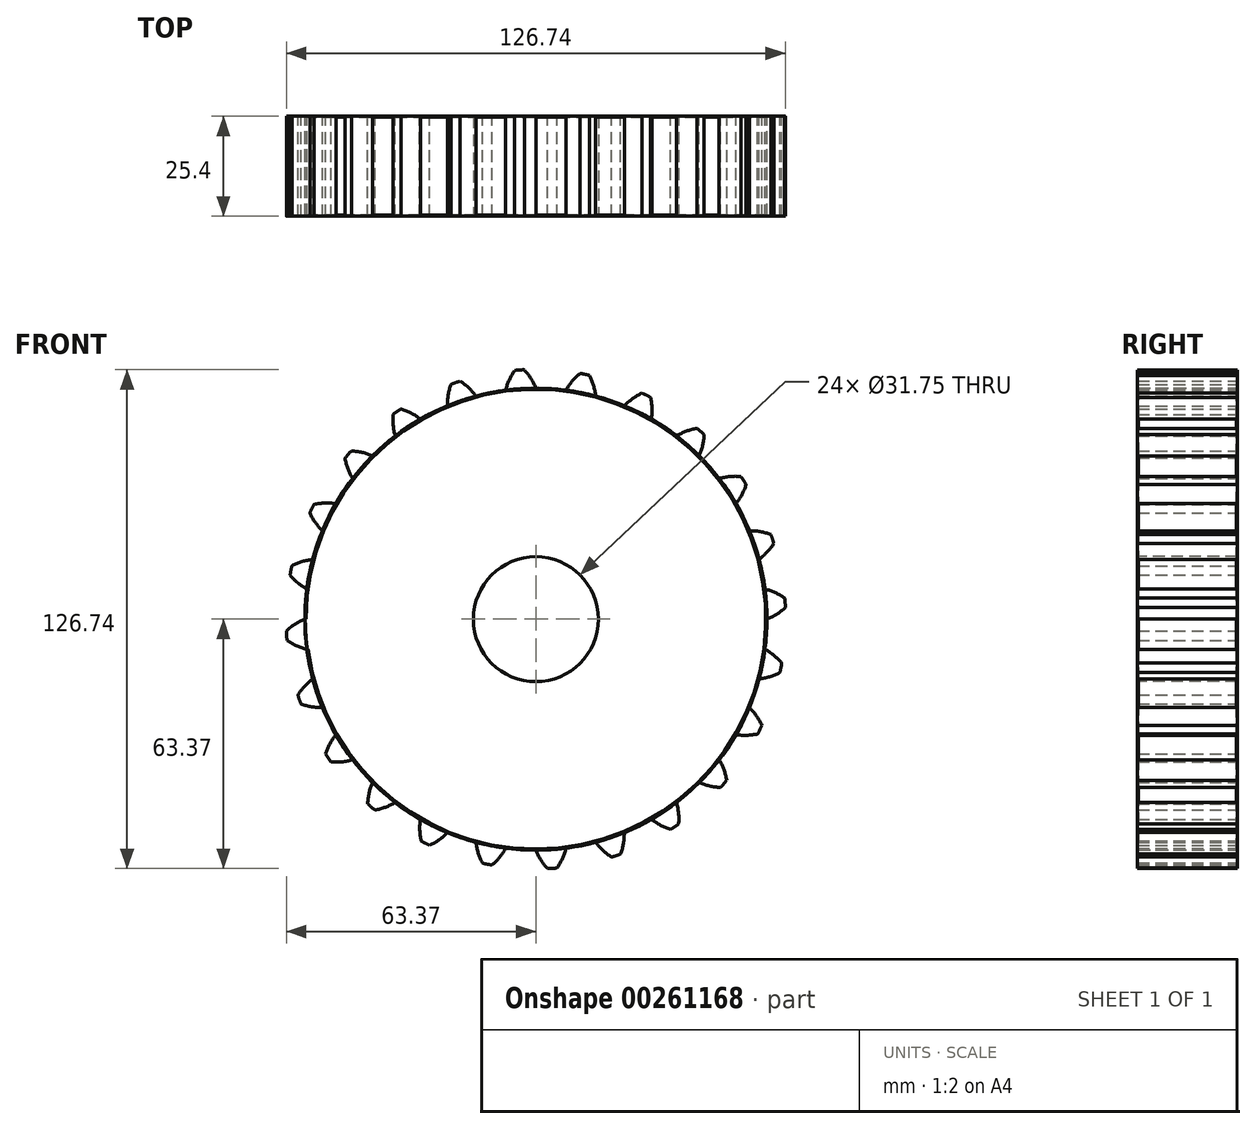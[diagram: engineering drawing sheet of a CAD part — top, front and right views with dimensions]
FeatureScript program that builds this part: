
annotation { "Feature Type Name" : "Feature", "Feature Type Description" : "" }
export const myFeature = defineFeature(function(context is Context, id is Id, definition is map)
    precondition{}
    {
        {
            var Q0;
            Q0=qCreatedBy(makeId("Front.planeOp"),FACE);
            var sketch = newSketch(context, id + "F0", { "sketchPlane" : qUnion([Q0])});
            skCircle(sketch, "E0", {"center": v(0, 0) * mm, "radius": 63.5 * mm, "construction": true});
            skCircle(sketch, "E1", {"center": v(0, 0) * mm, "radius": 53.72 * mm, "construction": true});
            skCircle(sketch, "E2", {"center": v(0, 0) * mm, "radius": 58.67 * mm});
            skLineSegment(sketch, "E3", {"start": v(0, 0) * mm, "end": v(0, 96.68) * mm, "construction": true});
            skLineSegment(sketch, "E4", {"start": v(0, 0) * mm, "end": v(-6.34, 96.72) * mm, "construction": true});
            skLineSegment(sketch, "E5", {"start": v(0, 58.67) * mm, "end": v(-75.78, 58.67) * mm, "construction": true});
            skLineSegment(sketch, "E6", {"start": v(0, 58.67) * mm, "end": v(-75.78, 31.1) * mm, "construction": true});
            skCircle(sketch, "E7", {"center": v(0, 0) * mm, "radius": 55.14 * mm, "construction": true});
            skCircle(sketch, "E8", {"center": v(0, 58.67) * mm, "radius": 14.6 * mm, "construction": true});
            skCircle(sketch, "E9", {"center": v(-13.63, 53.42) * mm, "radius": 14.6 * mm, "construction": true});
            skArc(sketch, "E10", {"start": v(0, 58.67) * mm, "mid": v(-1.24, 61.16) * mm, "end": v(-2.93, 63.37) * mm});
            skArc(sketch, "E11", {"start": v(0.97, 53.71) * mm, "mid": v(0.7, 56.24) * mm, "end": v(0, 58.67) * mm});
            skArc(sketch, "E12.MirrorCS", {"start": v(-7.66, 58.17) * mm, "mid": v(-6.75, 60.8) * mm, "end": v(-5.37, 63.2) * mm});
            skArc(sketch, "E13.MirrorCS", {"start": v(-7.98, 53.13) * mm, "mid": v(-8.04, 55.66) * mm, "end": v(-7.66, 58.17) * mm});
            skArc(sketch, "E14", {"start": v(-2.93, 63.37) * mm, "mid": v(-4.15, 63.34) * mm, "end": v(-5.37, 63.2) * mm});
            skSolve(sketch);
        }
        {
            var Q0;
            {var subQ0=sQuery(id+"F0.wireOp",EDGE,"E10");Q0=makeQuery(id+"F0.imprint","IMPRINT",FACE,{"disambiguationData":[TD([[makeQuery(id+"F0.imprint","IMPRINT",EDGE,{"derivedFrom":subQ0}),1.0]])]});}
            var Q1;
            {var subQ0=sQuery(id+"F0.wireOp",EDGE,"E2");var subQ1=makeQuery(id+"F0.imprint","INTERSECT",VERTEX,{"derivedFrom":[subQ0,sQuery(id+"F0.wireOp",EDGE,"E10")]});Q1=makeQuery(id+"F0.imprint","IMPRINT",FACE,{"disambiguationData":[TD([[makeQuery(id+"F0.imprint","IMPRINT",EDGE,{"disambiguationData":[TD([[subQ1,-1.0]])],"derivedFrom":subQ0}),1.0]])]});}
            extrude(context, id + "F1", {"entities" : qUnion([Q0, Q1]), "endBound" : BoundingType.SYMMETRIC, "depth" : 25.4 * mm});
        }
        {
            var Q0;
            Q0=makeQuery(id+"F1.opExtrude","SWEPT_BODY",BODY,{"disambiguationData":[OSD([sQuery(id+"F0.wireOp",EDGE,"E2"),sQuery(id+"F0.wireOp",EDGE,"E10"),sQuery(id+"F0.wireOp",EDGE,"E12.MirrorCS"),sQuery(id+"F0.wireOp",EDGE,"E14")])]});
            var Q1;
            Q1=makeQuery(id+"F1.opExtrude","SWEPT_FACE",FACE,{"disambiguationData":[OSD([sQuery(id+"F0.wireOp",EDGE,"E2")])]});
            circularPattern(context, id + "F2", {"entities" : qUnion([Q0]), "axis" : qUnion([Q1]), "angle" : 15 * degree, "instanceCount" : 24});
        }
        {
            var Q0;
            Q0=makeQuery(id+"F2.opPattern","COPY",FACE,{"derivedFrom":makeQuery(id+"F1.opExtrude","CAP_FACE",FACE,{"disambiguationData":[OSD([sQuery(id+"F0.wireOp",EDGE,"E2"),sQuery(id+"F0.wireOp",EDGE,"E10"),sQuery(id+"F0.wireOp",EDGE,"E12.MirrorCS"),sQuery(id+"F0.wireOp",EDGE,"E14")])],"isStart":false}),"instanceName":"12"});
            var sketch = newSketch(context, id + "F3", { "sketchPlane" : qUnion([Q0])});
            skCircle(sketch, "E15", {"center": v(0, 0) * mm, "radius": 15.24 * mm});
            skSolve(sketch);
        }
        {
            var Q0;
            Q0=sQuery(id+"F3.wireOp",VERTEX,"E15.center");
            var Q1;
            Q1=makeQuery(id+"F1.opExtrude","SWEPT_BODY",BODY,{"disambiguationData":[OSD([sQuery(id+"F0.wireOp",EDGE,"E2"),sQuery(id+"F0.wireOp",EDGE,"E10"),sQuery(id+"F0.wireOp",EDGE,"E12.MirrorCS"),sQuery(id+"F0.wireOp",EDGE,"E14")])]});
            var Q2;
            Q2=makeQuery(id+"F2.opPattern","COPY",BODY,{"derivedFrom":makeQuery(id+"F1.opExtrude","SWEPT_BODY",BODY,{"disambiguationData":[OSD([sQuery(id+"F0.wireOp",EDGE,"E2"),sQuery(id+"F0.wireOp",EDGE,"E10"),sQuery(id+"F0.wireOp",EDGE,"E12.MirrorCS"),sQuery(id+"F0.wireOp",EDGE,"E14")])]}),"instanceName":"1"});
            var Q3;
            Q3=makeQuery(id+"F2.opPattern","COPY",BODY,{"derivedFrom":makeQuery(id+"F1.opExtrude","SWEPT_BODY",BODY,{"disambiguationData":[OSD([sQuery(id+"F0.wireOp",EDGE,"E2"),sQuery(id+"F0.wireOp",EDGE,"E10"),sQuery(id+"F0.wireOp",EDGE,"E12.MirrorCS"),sQuery(id+"F0.wireOp",EDGE,"E14")])]}),"instanceName":"2"});
            var Q4;
            Q4=makeQuery(id+"F2.opPattern","COPY",BODY,{"derivedFrom":makeQuery(id+"F1.opExtrude","SWEPT_BODY",BODY,{"disambiguationData":[OSD([sQuery(id+"F0.wireOp",EDGE,"E2"),sQuery(id+"F0.wireOp",EDGE,"E10"),sQuery(id+"F0.wireOp",EDGE,"E12.MirrorCS"),sQuery(id+"F0.wireOp",EDGE,"E14")])]}),"instanceName":"3"});
            var Q5;
            Q5=makeQuery(id+"F2.opPattern","COPY",BODY,{"derivedFrom":makeQuery(id+"F1.opExtrude","SWEPT_BODY",BODY,{"disambiguationData":[OSD([sQuery(id+"F0.wireOp",EDGE,"E2"),sQuery(id+"F0.wireOp",EDGE,"E10"),sQuery(id+"F0.wireOp",EDGE,"E12.MirrorCS"),sQuery(id+"F0.wireOp",EDGE,"E14")])]}),"instanceName":"4"});
            var Q6;
            Q6=makeQuery(id+"F2.opPattern","COPY",BODY,{"derivedFrom":makeQuery(id+"F1.opExtrude","SWEPT_BODY",BODY,{"disambiguationData":[OSD([sQuery(id+"F0.wireOp",EDGE,"E2"),sQuery(id+"F0.wireOp",EDGE,"E10"),sQuery(id+"F0.wireOp",EDGE,"E12.MirrorCS"),sQuery(id+"F0.wireOp",EDGE,"E14")])]}),"instanceName":"5"});
            var Q7;
            Q7=makeQuery(id+"F2.opPattern","COPY",BODY,{"derivedFrom":makeQuery(id+"F1.opExtrude","SWEPT_BODY",BODY,{"disambiguationData":[OSD([sQuery(id+"F0.wireOp",EDGE,"E2"),sQuery(id+"F0.wireOp",EDGE,"E10"),sQuery(id+"F0.wireOp",EDGE,"E12.MirrorCS"),sQuery(id+"F0.wireOp",EDGE,"E14")])]}),"instanceName":"6"});
            var Q8;
            Q8=makeQuery(id+"F2.opPattern","COPY",BODY,{"derivedFrom":makeQuery(id+"F1.opExtrude","SWEPT_BODY",BODY,{"disambiguationData":[OSD([sQuery(id+"F0.wireOp",EDGE,"E2"),sQuery(id+"F0.wireOp",EDGE,"E10"),sQuery(id+"F0.wireOp",EDGE,"E12.MirrorCS"),sQuery(id+"F0.wireOp",EDGE,"E14")])]}),"instanceName":"7"});
            var Q9;
            Q9=makeQuery(id+"F2.opPattern","COPY",BODY,{"derivedFrom":makeQuery(id+"F1.opExtrude","SWEPT_BODY",BODY,{"disambiguationData":[OSD([sQuery(id+"F0.wireOp",EDGE,"E2"),sQuery(id+"F0.wireOp",EDGE,"E10"),sQuery(id+"F0.wireOp",EDGE,"E12.MirrorCS"),sQuery(id+"F0.wireOp",EDGE,"E14")])]}),"instanceName":"8"});
            var Q10;
            Q10=makeQuery(id+"F2.opPattern","COPY",BODY,{"derivedFrom":makeQuery(id+"F1.opExtrude","SWEPT_BODY",BODY,{"disambiguationData":[OSD([sQuery(id+"F0.wireOp",EDGE,"E2"),sQuery(id+"F0.wireOp",EDGE,"E10"),sQuery(id+"F0.wireOp",EDGE,"E12.MirrorCS"),sQuery(id+"F0.wireOp",EDGE,"E14")])]}),"instanceName":"9"});
            var Q11;
            Q11=makeQuery(id+"F2.opPattern","COPY",BODY,{"derivedFrom":makeQuery(id+"F1.opExtrude","SWEPT_BODY",BODY,{"disambiguationData":[OSD([sQuery(id+"F0.wireOp",EDGE,"E2"),sQuery(id+"F0.wireOp",EDGE,"E10"),sQuery(id+"F0.wireOp",EDGE,"E12.MirrorCS"),sQuery(id+"F0.wireOp",EDGE,"E14")])]}),"instanceName":"10"});
            var Q12;
            Q12=makeQuery(id+"F2.opPattern","COPY",BODY,{"derivedFrom":makeQuery(id+"F1.opExtrude","SWEPT_BODY",BODY,{"disambiguationData":[OSD([sQuery(id+"F0.wireOp",EDGE,"E2"),sQuery(id+"F0.wireOp",EDGE,"E10"),sQuery(id+"F0.wireOp",EDGE,"E12.MirrorCS"),sQuery(id+"F0.wireOp",EDGE,"E14")])]}),"instanceName":"11"});
            var Q13;
            Q13=makeQuery(id+"F2.opPattern","COPY",BODY,{"derivedFrom":makeQuery(id+"F1.opExtrude","SWEPT_BODY",BODY,{"disambiguationData":[OSD([sQuery(id+"F0.wireOp",EDGE,"E2"),sQuery(id+"F0.wireOp",EDGE,"E10"),sQuery(id+"F0.wireOp",EDGE,"E12.MirrorCS"),sQuery(id+"F0.wireOp",EDGE,"E14")])]}),"instanceName":"12"});
            var Q14;
            Q14=makeQuery(id+"F2.opPattern","COPY",BODY,{"derivedFrom":makeQuery(id+"F1.opExtrude","SWEPT_BODY",BODY,{"disambiguationData":[OSD([sQuery(id+"F0.wireOp",EDGE,"E2"),sQuery(id+"F0.wireOp",EDGE,"E10"),sQuery(id+"F0.wireOp",EDGE,"E12.MirrorCS"),sQuery(id+"F0.wireOp",EDGE,"E14")])]}),"instanceName":"13"});
            var Q15;
            Q15=makeQuery(id+"F2.opPattern","COPY",BODY,{"derivedFrom":makeQuery(id+"F1.opExtrude","SWEPT_BODY",BODY,{"disambiguationData":[OSD([sQuery(id+"F0.wireOp",EDGE,"E2"),sQuery(id+"F0.wireOp",EDGE,"E10"),sQuery(id+"F0.wireOp",EDGE,"E12.MirrorCS"),sQuery(id+"F0.wireOp",EDGE,"E14")])]}),"instanceName":"14"});
            var Q16;
            Q16=makeQuery(id+"F2.opPattern","COPY",BODY,{"derivedFrom":makeQuery(id+"F1.opExtrude","SWEPT_BODY",BODY,{"disambiguationData":[OSD([sQuery(id+"F0.wireOp",EDGE,"E2"),sQuery(id+"F0.wireOp",EDGE,"E10"),sQuery(id+"F0.wireOp",EDGE,"E12.MirrorCS"),sQuery(id+"F0.wireOp",EDGE,"E14")])]}),"instanceName":"15"});
            var Q17;
            Q17=makeQuery(id+"F2.opPattern","COPY",BODY,{"derivedFrom":makeQuery(id+"F1.opExtrude","SWEPT_BODY",BODY,{"disambiguationData":[OSD([sQuery(id+"F0.wireOp",EDGE,"E2"),sQuery(id+"F0.wireOp",EDGE,"E10"),sQuery(id+"F0.wireOp",EDGE,"E12.MirrorCS"),sQuery(id+"F0.wireOp",EDGE,"E14")])]}),"instanceName":"16"});
            var Q18;
            Q18=makeQuery(id+"F2.opPattern","COPY",BODY,{"derivedFrom":makeQuery(id+"F1.opExtrude","SWEPT_BODY",BODY,{"disambiguationData":[OSD([sQuery(id+"F0.wireOp",EDGE,"E2"),sQuery(id+"F0.wireOp",EDGE,"E10"),sQuery(id+"F0.wireOp",EDGE,"E12.MirrorCS"),sQuery(id+"F0.wireOp",EDGE,"E14")])]}),"instanceName":"17"});
            var Q19;
            Q19=makeQuery(id+"F2.opPattern","COPY",BODY,{"derivedFrom":makeQuery(id+"F1.opExtrude","SWEPT_BODY",BODY,{"disambiguationData":[OSD([sQuery(id+"F0.wireOp",EDGE,"E2"),sQuery(id+"F0.wireOp",EDGE,"E10"),sQuery(id+"F0.wireOp",EDGE,"E12.MirrorCS"),sQuery(id+"F0.wireOp",EDGE,"E14")])]}),"instanceName":"18"});
            var Q20;
            Q20=makeQuery(id+"F2.opPattern","COPY",BODY,{"derivedFrom":makeQuery(id+"F1.opExtrude","SWEPT_BODY",BODY,{"disambiguationData":[OSD([sQuery(id+"F0.wireOp",EDGE,"E2"),sQuery(id+"F0.wireOp",EDGE,"E10"),sQuery(id+"F0.wireOp",EDGE,"E12.MirrorCS"),sQuery(id+"F0.wireOp",EDGE,"E14")])]}),"instanceName":"19"});
            var Q21;
            Q21=makeQuery(id+"F2.opPattern","COPY",BODY,{"derivedFrom":makeQuery(id+"F1.opExtrude","SWEPT_BODY",BODY,{"disambiguationData":[OSD([sQuery(id+"F0.wireOp",EDGE,"E2"),sQuery(id+"F0.wireOp",EDGE,"E10"),sQuery(id+"F0.wireOp",EDGE,"E12.MirrorCS"),sQuery(id+"F0.wireOp",EDGE,"E14")])]}),"instanceName":"20"});
            var Q22;
            Q22=makeQuery(id+"F2.opPattern","COPY",BODY,{"derivedFrom":makeQuery(id+"F1.opExtrude","SWEPT_BODY",BODY,{"disambiguationData":[OSD([sQuery(id+"F0.wireOp",EDGE,"E2"),sQuery(id+"F0.wireOp",EDGE,"E10"),sQuery(id+"F0.wireOp",EDGE,"E12.MirrorCS"),sQuery(id+"F0.wireOp",EDGE,"E14")])]}),"instanceName":"21"});
            var Q23;
            Q23=makeQuery(id+"F2.opPattern","COPY",BODY,{"derivedFrom":makeQuery(id+"F1.opExtrude","SWEPT_BODY",BODY,{"disambiguationData":[OSD([sQuery(id+"F0.wireOp",EDGE,"E2"),sQuery(id+"F0.wireOp",EDGE,"E10"),sQuery(id+"F0.wireOp",EDGE,"E12.MirrorCS"),sQuery(id+"F0.wireOp",EDGE,"E14")])]}),"instanceName":"22"});
            var Q24;
            Q24=makeQuery(id+"F2.opPattern","COPY",BODY,{"derivedFrom":makeQuery(id+"F1.opExtrude","SWEPT_BODY",BODY,{"disambiguationData":[OSD([sQuery(id+"F0.wireOp",EDGE,"E2"),sQuery(id+"F0.wireOp",EDGE,"E10"),sQuery(id+"F0.wireOp",EDGE,"E12.MirrorCS"),sQuery(id+"F0.wireOp",EDGE,"E14")])]}),"instanceName":"23"});
            hole(context, id + "F4", {"style" : HoleStyle.SIMPLE, "endStyle" : HoleEndStyle.THROUGH, "holeDiameter" : 31.75 * mm, "tappedDepth" : 12.7 * mm, "tapClearance" : 3, "locations" : qUnion([Q0]), "scope" : qUnion([Q1, Q2, Q3, Q4, Q5, Q6, Q7, Q8, Q9, Q10, Q11, Q12, Q13, Q14, Q15, Q16, Q17, Q18, Q19, Q20, Q21, Q22, Q23, Q24])});
        }
        {
            var Q0;
            Q0=makeQuery(id+"F2.opPattern","COPY",EDGE,{"derivedFrom":makeQuery(id+"F1.opExtrude","CAP_EDGE",EDGE,{"disambiguationData":[OSD([sQuery(id+"F0.wireOp",EDGE,"E2")])],"isStart":false}),"instanceName":"18"});
            var Q1;
            Q1=makeQuery(id+"F2.opPattern","COPY",EDGE,{"derivedFrom":makeQuery(id+"F1.opExtrude","CAP_EDGE",EDGE,{"disambiguationData":[OSD([sQuery(id+"F0.wireOp",EDGE,"E2")])],"isStart":true}),"instanceName":"23"});
            chamfer(context, id + "F5", {"entities" : qUnion([Q0, Q1]), "width" : 0.25 * mm, "tangentPropagation" : true});
        }
    });
